# Revit family: Ginko 4.0 cons
name_source: partatom
category: Lighting Fixtures
units: mm (PartAtom-declared; Revit-internal decimal feet)

## family parameters
Always vertical = No
Cut with Voids When Loaded = No
Light Source = No
OmniClass Number = 23.80.70.00
OmniClass Title = Lighting
Part Type = Normal
Room Calculation Point = Yes
Round Connector Dimension = Use Diameter
Shared = No
Work Plane-Based = Yes

## types (7) — shared parameters
Apparent Load Phase 1 = 5 W
Body = L&L_Anticorodal aluminium
Braket = L&L_Steel inox AISI 316L
CRI = CRI 80, CRI >90
Code = -
Control system = ON/OFF
Cutout dimensions = -
Default Elevation = 1219 mm
Delivered lumen output = 1724 lm (3000K, 12°, CRI >90), 2133 lm (3000K, 12°, CRI 80)
Description = projector for outdoor applications
Energy efficiency class = A A+ A++
Features = 13°x65°, 24°x69° optics adjustable through 360° using the magnet provided
Geometry = Ginko 4.0_movable : Ginko 4.0
H1 = 105 mm  [stored 0.344488 ft]
Height mm = 215 mm  [stored 0.705381 ft]
Horizontal rotation max = 190.00°
IP = IP66
LED Colour = 2700K, 3000K, 4000K
Length mm = 110 mm  [stored 0.360892 ft]
Lens = L&L_Tempered extra-clear glass
Lumen output at source = 1860 lm (3000K, CRI >90), 2302 lm (3000K, CRI 80)
Manufacturer = L&L Luce&Light
Material = body in anticorodal aluminium, AISI 316L stainless steel bracket, screen in serigraphed, tempered, transparent extra-clear glass
Model = Ginko 4.0
Mounting = surface mounted (ceiling, wall, ground, spike)
No. and type of led = 1 high power density COB LED, 2-step MacAdam, 50 000h L95 B10 (Ta 25°C)
Notes = version with bracket in customized length available on request
Power = 25W
Power cables = includes 1.50/5/10/15/20 m neoprene cable H05RN-F 2x0.75/0.75 Ø6.3 mm
Power supply = 24Vdc
Power supply unit = not included
Trim = Luce&Light_Black Aluminum
URL = https://www.lucelight.it
URL Accessories and power supply units = https://www.lucelight.it
URL Catalogue = https://www.lucelight.it
URL DXF = https://www.lucelight.it
URL Description = https://www.lucelight.it
URL General code = https://www.lucelight.it
URL IES Photometric file = https://www.lucelight.it
URL Image = https://www.lucelight.it
Vertical rotation max = 360.00°
Weight kg = 2.10 kg
Width mm = 109 mm
Wiring = parallel
X1 = 100 mm  [stored 0.328084 ft]

## per-type parameters (varying)
| type | Light Source Ginko 4.0 | Optics |
| Ginko 4.0 S 12°  (3000K 25W 24Vdc) | Light sourse Ginko 4.0 : S 12° | 12° |
| Ginko 4.0 M 26°  (3000K 25W 24Vdc) | Light sourse Ginko 4.0 : M 26 | 26° |
| Ginko 4.0 L 34°  (3000K 25W 24Vdc) | Light sourse Ginko 4.0 : L 34° | 34° |
| Ginko 4.0 J 55°  (3000K 25W 24Vdc) | Light sourse Ginko 4.0 : J 55° | 55° |
| Ginko 4.0 Adjustable 13°x65°  (3000K 25W 24Vdc) | Light sourse Ginko 4.0 : Adjustable 13°x65° | Adjustable 13°x65° |
| Ginko 4.0 Adjustable 24°x69°  (3000K 25W 24Vdc) | Light sourse Ginko 4.0 : Adjustable 24°x69° | Adjustable 24°x69° |
| Ginko 4.0 P 38°  (3000K 25W 24Vdc) | Light sourse Ginko 4.0 : Sharp 38° | Sharp 38° |

note: [stored X ft] marks values corroborated as IEEE doubles in the binary element streams (Revit-internal decimal feet)

## geometry (parser evidence)
native form markers: Blend x6, Sweep x17
no freeform markers — native parametric forms only
